# Revit family: WCSeatCover-Duroplast-SoftClosing-Vitra-DlightSeries_123-003-009
name_source: partatom
category: Plumbing Fixtures
revit_build: Autodesk Revit 2017 (Build: 20160225_1515(x64)
units: mm (PartAtom-declared; Revit-internal decimal feet)

## family parameters
Cut with Voids When Loaded = No
Host = Face
OmniClass Number = 23.45.05.21
OmniClass Title = Plumbing Fixtures - Sanitary Disposal Units
Part Type = Normal
Room Calculation Point = No
Round Connector Dimension = Use Diameter
Shared = Yes

## types (1)
- WCSeatCover-Duroplast-Vitra-DlightSeries_123-003-009
    Article No. (default) = 123-003-009
    BIMobject category = Sanitary - Toilet Seats
    CW Connection = No
    Color = White
    Cost = 0 $
    Default Elevation = 410 mm  [stored 1.34514 ft]
    Description = VitrA DLight WC Seat
    Design country = Turkey
    HW Connection = No
    IFC Classification = Sanitary Terminal
    Main Material = Duroplast
    Manufacturer = Vitra
    Manufacturer name = Vitra
    Model = 123-003-009
    NBS Referans Code = 35-93-95
    NBS Referans Description = Wc Seats And Covers
    Nominal Depth (mm) = 450 mm  [stored 1.47638 ft]
    Nominal Height (mm) = 50 mm  [stored 0.164042 ft]
    Nominal Width (mm) = 370 mm  [stored 1.21391 ft]
    OmniClass Code = 23-31 19 19 11
    OmniClass Description = Toilets
    Product Manual = WC Seat - Duroplast
    Product SKU = 123-003-009
    Product certification = https://vitraglobal.com
    Product data url = https://www.vitra.com.tr
    Product family = Dlight
    Secondary Material = White
    Technical description = https://www.vitra.com.tr
    UNSPSC Code = 35-93-95
    UNSPSC Description = Water Operated Water Closets
    URL = https://www.vitra.com.tr
    Uniclass 1.4 Code = L72164
    Uniclass 1.4 Description = Toilets
    Uniclass 2.0 Code = PR-35-93-95
    Uniclass 2.0 Description = Wc Seats And Covers
    Uniclass 2015 Code = Pr_40_20_93_95
    Uniclass 2015 Name = WC seats and covers
    Vent Connection = No
    Warranty Period (Year) = 2 Years
    Waste Connection = No
    Weight Net (kg) = 3,100
    Youtube = https://www.youtube.com

note: [stored X ft] marks values corroborated as IEEE doubles in the binary element streams (Revit-internal decimal feet)

## geometry (parser evidence)
native form markers: Sweep x3
no freeform markers — native parametric forms only
